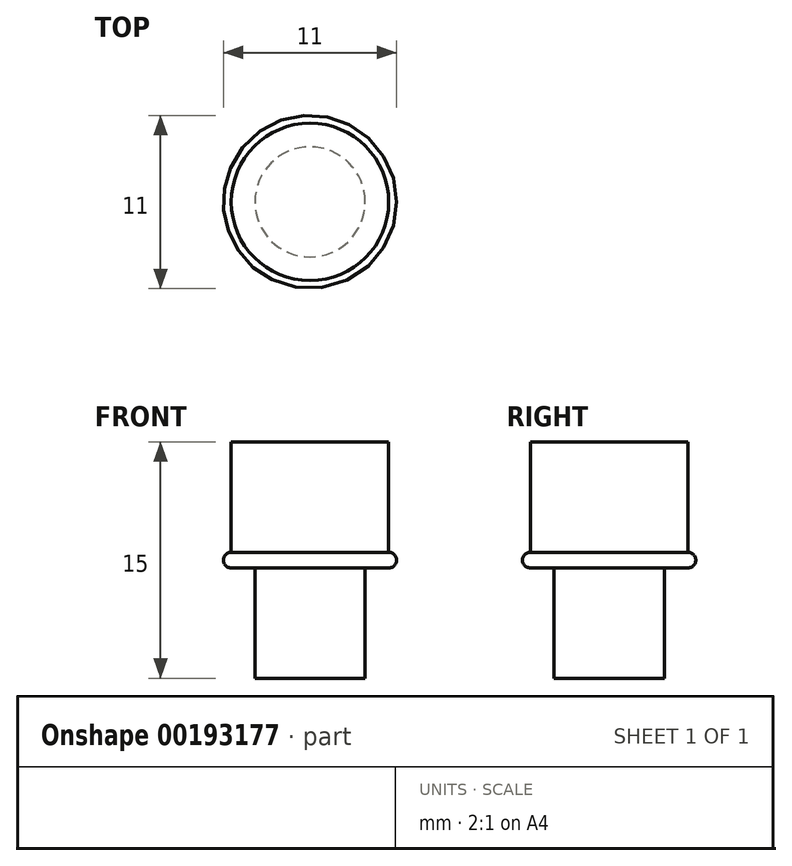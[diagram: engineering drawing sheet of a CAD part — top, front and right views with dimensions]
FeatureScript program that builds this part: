
annotation { "Feature Type Name" : "Feature", "Feature Type Description" : "" }
export const myFeature = defineFeature(function(context is Context, id is Id, definition is map)
    precondition{}
    {
        {
            var Q0;
            Q0=qCreatedBy(makeId("Top.planeOp"),FACE);
            var sketch = newSketch(context, id + "F0", { "sketchPlane" : qUnion([Q0])});
            skCircle(sketch, "E0", {"center": v(0, 0) * mm, "radius": 3.5 * mm});
            skSolve(sketch);
        }
        {
            var Q0;
            Q0 = qSketchRegion(id + "F0", true);
            extrude(context, id + "F1", {"entities" : qUnion([Q0]), "depth" : 7 * mm});
        }
        {
            var Q0;
            Q0=makeQuery(id+"F1.opExtrude","CAP_FACE",FACE,{"disambiguationData":[OSD([sQuery(id+"F0.wireOp",EDGE,"E0")])],"isStart":false});
            var sketch = newSketch(context, id + "F2", { "sketchPlane" : qUnion([Q0])});
            skCircle(sketch, "E1", {"center": v(0, 0) * mm, "radius": 5.5 * mm});
            skSolve(sketch);
        }
        {
            var Q0;
            Q0 = qSketchRegion(id + "F2", true);
            extrude(context, id + "F3", {"entities" : qUnion([Q0]), "operationType" : NewBodyOperationType.ADD, "depth" : 1 * mm});
        }
        {
            var Q0;
            Q0=makeQuery(id+"F3.opExtrude","CAP_FACE",FACE,{"disambiguationData":[OSD([sQuery(id+"F2.wireOp",EDGE,"E1")])],"isStart":false});
            var sketch = newSketch(context, id + "F4", { "sketchPlane" : qUnion([Q0])});
            skCircle(sketch, "E2", {"center": v(0, 0) * mm, "radius": 5 * mm});
            skSolve(sketch);
        }
        {
            var Q0;
            Q0=makeQuery(id+"F3.opExtrude","CAP_EDGE",EDGE,{"disambiguationData":[OSD([sQuery(id+"F2.wireOp",EDGE,"E1")])],"isStart":false});
            var Q1;
            Q1=makeQuery(id+"F3.opExtrude","CAP_EDGE",EDGE,{"disambiguationData":[OSD([sQuery(id+"F2.wireOp",EDGE,"E1")])],"isStart":true});
            fillet(context, id + "F5", {"entities" : qUnion([Q0, Q1]), "radius" : 0.5 * mm, "tangentPropagation" : true, "allowEdgeOverflow" : false});
        }
        {
            var Q0;
            Q0 = qSketchRegion(id + "F4", true);
            extrude(context, id + "F6", {"entities" : qUnion([Q0]), "operationType" : NewBodyOperationType.ADD, "depth" : 7 * mm});
        }
    });
